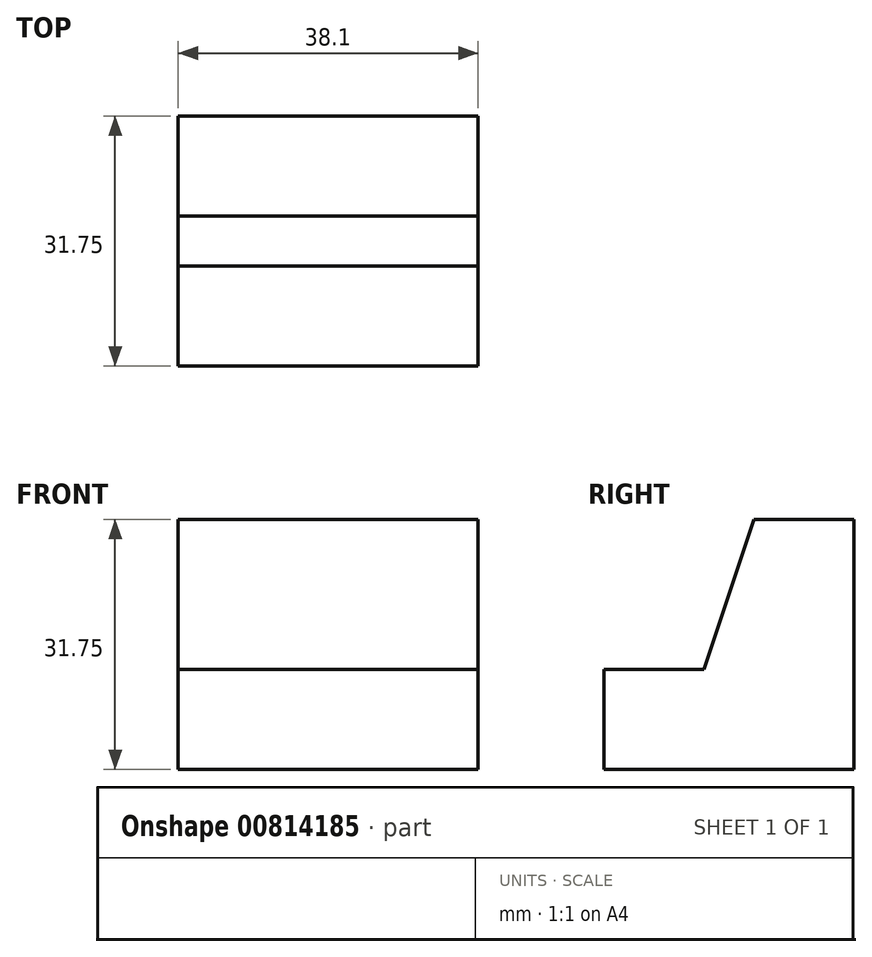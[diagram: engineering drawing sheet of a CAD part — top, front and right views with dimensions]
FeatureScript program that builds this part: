
annotation { "Feature Type Name" : "Feature", "Feature Type Description" : "" }
export const myFeature = defineFeature(function(context is Context, id is Id, definition is map)
    precondition{}
    {
        {
            var Q0;
            Q0=qCreatedBy(makeId("Top.planeOp"),FACE);
            var sketch = newSketch(context, id + "F0", { "sketchPlane" : qUnion([Q0])});
            skLineSegment(sketch, "E0", {"start": v(0, 0) * mm, "end": v(0, 31.75) * mm});
            skLineSegment(sketch, "E1", {"start": v(0, 0) * mm, "end": v(38.1, 0) * mm});
            skLineSegment(sketch, "E2", {"start": v(38.1, 0) * mm, "end": v(38.1, 31.75) * mm});
            skLineSegment(sketch, "E3", {"start": v(0, 31.75) * mm, "end": v(38.1, 31.75) * mm});
            skSolve(sketch);
        }
        {
            var Q0;
            Q0 = qSketchRegion(id + "F0", true);
            extrude(context, id + "F1", {"entities" : qUnion([Q0]), "depth" : 31.75 * mm, "offsetDistance" : 25.4 * mm});
        }
        {
            var Q0;
            Q0=makeQuery(id+"F1.opExtrude","SWEPT_FACE",FACE,{"disambiguationData":[OSD([sQuery(id+"F0.wireOp",EDGE,"E2")])]});
            var sketch = newSketch(context, id + "F2", { "sketchPlane" : qUnion([Q0])});
            skLineSegment(sketch, "E4", {"start": v(31.75, 31.75) * mm, "end": v(19.05, 31.75) * mm});
            skLineSegment(sketch, "E5", {"start": v(0, 0) * mm, "end": v(0, 12.7) * mm});
            skLineSegment(sketch, "E6", {"start": v(0, 12.7) * mm, "end": v(12.7, 12.7) * mm});
            skLineSegment(sketch, "E7", {"start": v(19.05, 31.75) * mm, "end": v(12.7, 12.7) * mm});
            skSolve(sketch);
        }
        {
            var Q0;
            Q0 = qSketchRegion(id + "F2", true);
            var Q1;
            {var subQ0=sQuery(id+"F2.wireOp",EDGE,"E6");Q1=makeQuery(id+"F2.imprint","IMPRINT",FACE,{"disambiguationData":[TD([[makeQuery(id+"F2.imprint","IMPRINT",EDGE,{"derivedFrom":subQ0}),1.0]])]});}
            extrude(context, id + "F3", {"entities" : qUnion([Q0, Q1]), "operationType" : NewBodyOperationType.REMOVE, "oppositeDirection" : true, "depth" : 38.1 * mm, "offsetDistance" : 25.4 * mm});
        }
    });
